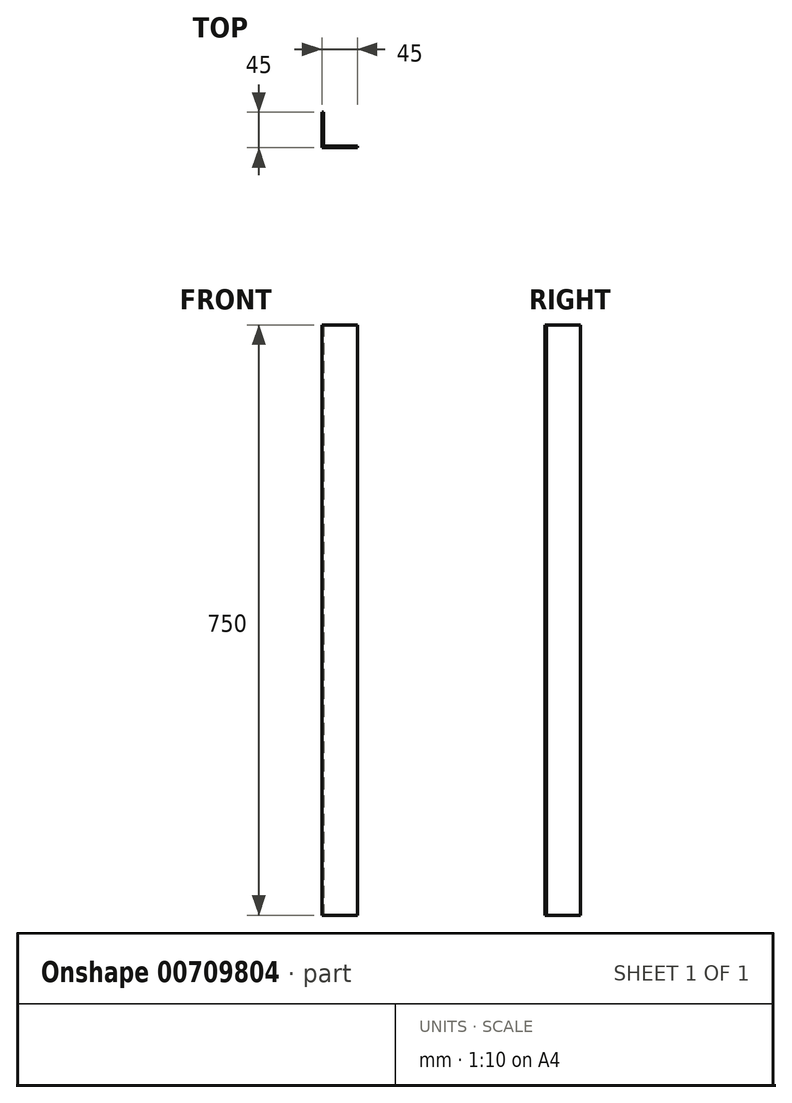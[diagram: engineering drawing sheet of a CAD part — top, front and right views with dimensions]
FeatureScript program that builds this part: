
annotation { "Feature Type Name" : "Feature", "Feature Type Description" : "" }
export const myFeature = defineFeature(function(context is Context, id is Id, definition is map)
    precondition{}
    {
        {
            var Q0;
            Q0=qCreatedBy(makeId("Top.planeOp"),FACE);
            var sketch = newSketch(context, id + "F0", { "sketchPlane" : qUnion([Q0])});
            skLineSegment(sketch, "E0.bottom", {"start": v(0, 0) * mm, "end": v(-45, 0) * mm});
            skLineSegment(sketch, "E0.top", {"start": v(-43, 45) * mm, "end": v(-45, 45) * mm});
            skLineSegment(sketch, "E0.left", {"start": v(0, 0) * mm, "end": v(0, 2) * mm});
            skLineSegment(sketch, "E0.right", {"start": v(-45, 0) * mm, "end": v(-45, 45) * mm});
            skLineSegment(sketch, "E1.2", {"start": v(0, 2) * mm, "end": v(-43, 2) * mm});
            skLineSegment(sketch, "E1.3", {"start": v(-43, 2) * mm, "end": v(-43, 45) * mm});
            skSolve(sketch);
        }
        {
            var Q0;
            Q0=makeQuery(id+"F0.imprint","IMPRINT",FACE,{"disambiguationData":[TD([[makeQuery(id+"F0.imprint","IMPRINT",EDGE,{"derivedFrom":sQuery(id+"F0.wireOp",EDGE,"E0.bottom")}),-1.0]])]});
            extrude(context, id + "F1", {"entities" : qUnion([Q0]), "depth" : 750 * mm, "offsetDistance" : 25 * mm});
        }
    });
